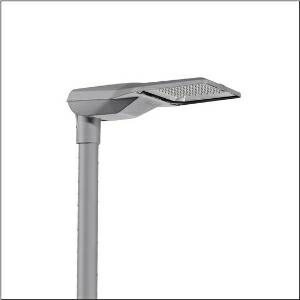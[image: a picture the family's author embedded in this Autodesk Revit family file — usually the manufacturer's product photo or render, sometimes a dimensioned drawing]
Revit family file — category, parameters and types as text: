
# Revit family: streetlight_sl_21_iq_midi___pl52_5xe3h31d08mb_2c0b
name_source: partatom
category: Lighting Fixtures
units: mm (PartAtom-declared; Revit-internal decimal feet)

## family parameters
Cut with Voids When Loaded = No
Host = Face
Light Source = No
Part Type = Normal
Room Calculation Point = No
Round Connector Dimension = Use Diameter
Shared = No

## types (1)
- --- (1 x LED, 19170 lm, 146.7 W, 3000K)
    Apparent Load = 147 VA
    CIE Flux Codes = 27 59 98 100 100
    Color Rendering = 70
    Color Temperature = 3000K
    Default Elevation = 1800 mm
    Description = Streetlight SL 21 iQ midi, mast luminaire, primary light control with lens, of PMMA, primary optical cover: cover, of toughened safety glass, transparent, light distribution: PL52, light emission: direct distribution, primary light characteristic: asymmetric, installation type: post-top, side-entry, LED, High Power LED, rated luminous flux: 19.170lm, luminous efficacy: 131lm/W, light colour: 730, colour temperature: 3000K, control gear: iQ-Comfort, control: Auto-Match, Temp-Guard, Lumen-Switch, Night-Set, Smart-Wire, Light-Fading, Desk-Remote (wireless, voltage-free reading and setting of iQ features in the workshop via application-optimized NFC function/RFID function), optimised constant luminous flux control (CLO 2.0), pre-setting: linear dimming characteristic, mains connection: 230..240V, AC, 50/60Hz, start of lifetime: 147W, end of service life: 161W, reduction: 62W, luminaire housing, of diecast aluminium, powder-coated, SITECO metallic grey (DB 702S), corrosivity category C5 high according to DIN EN ISO 12944, please order mast flange separately, inclination adjustable: 0°, 5°, 10°, 15°, sealing non-destructively replaceable, multi-level sealing system, length: 644mm, width: 335mm, height: 110mm, mast flange for spigot size: 42mm (side-entry): 5XC10008XM4, 60/48mm (side-entry/post-top): 5XC10108XM2, 76/60mm (side-entry/post-top): 5XC10108XM1, mounting height: 4..8m, protection rating (complete): IP66, insulation class (complete): insulation class II (safety insulation), certification: CE, ENEC, ENEC+, VDE, impact resistance: IK10, permissible operating ambient temperature for outdoor applications: -40..+50°C, standard-compliant lighting for roads and squares, packaging unit: 1 piece

Light Distribution: PL52
    Height = 111 mm
    Lamp = 1 x LED
    Lamp Light Flux = 19170 lm
    Lamp Power = 146.7 W
    Lamp count = 1
    Length = 644 mm
    Luminous efficacy = 131 lm/W
    Manufacturer = Siteco
    ModVariant = No
    Model = 5XE3H31D08MB
    Number of Poles = 1
    OnlyDefault = Yes
    Power Factor = 1
    Product Name = Streetlight SL 21 iQ midi | PL52
    Product group = mast luminaire | pylon top
    ProductGroupID = 6100
    Protection Class = Protection class II
    Protection Degree = IP 66
    RLX_Detail_Level = 1
    RLX_Emergency_Light_Flux = 0 lm
    RLX_Emergency_Type = 0
    RLX_Emergency_Type_DB = No
    RlxData = <blob elided: 36533 chars, md5=aeb7b0ed>
    Socket = socket
    Standby Power = 0 W
    System Light Flux = 19169 lm
    System Power = 147 W
    Type Comments = factory setting: luminous flux: 100 % | dim-lin: 254 | 753 mA
    Type Image = l_1004298.jpg
    URL = http://relux.com
    VarID = @adj_188281
    Voltage = 0 V
    Weight = 0.00 kg
    Width = 336 mm

## geometry (parser evidence)
native form markers: Blend x4, Sweep x9
no freeform markers — native parametric forms only
